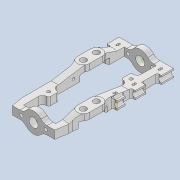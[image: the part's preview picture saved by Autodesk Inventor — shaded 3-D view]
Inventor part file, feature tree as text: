
AUTODESK INVENTOR PART (.ipt)
format: ipt  version: 2020 (Build 240168000, 168)  size: 925,184 bytes
history: native  units: mm
features: projected_geometry x23, sketch x22, extrude x20, thicken_offset x10, fillet x10, chamfer x7, other x5, plane x3, reference x3, hole x2
ambient origin geometry x8: Origin, YZ Plane, XZ Plane, XY Plane, X Axis, Y Axis, Z Axis, Center Point
bodies: Solid1 (feature_tree)
feature tree (105):
  extrude  "Extrusion1"  Depth=4.0mm
  plane  "Work Plane1"
  extrude  "Extrusion2"  Depth=2.0mm TaperAngle=0.0deg
  extrude  "Extrusion3"  Depth=4.0mm
  extrude  "Extrusion4"  Depth=2.0mm TaperAngle=0.0deg
  hole  "Hole1"  [1 undecoded]
  thicken_offset  "Thicken1"
  thicken_offset  "Thicken2"
  thicken_offset  "Thicken3"
  thicken_offset  "Thicken4"
  extrude  "Extrusion5"  Depth=3.0mm
  extrude  "Extrusion6"  Depth=2.0mm
  extrude  "Extrusion8"  Depth=6.0mm
  extrude  "Extrusion9"  Depth=3.5mm
  extrude  "Extrusion11"  Depth=3.5mm
  hole  "Hole2"  [1 undecoded]
  extrude  "Extrusion15"  Depth=3.5mm
  extrude  "Extrusion16"  Depth=3.5mm
  chamfer  "Chamfer1"  Distance=6.0mm
  chamfer  "Chamfer2"  Distance=2.0mm
  chamfer  "Chamfer3"  Distance=7.5mm
  chamfer  "Chamfer4"  Distance=9.0mm
  fillet  "Fillet4"  Radius=2.0mm
  fillet  "Fillet5"  Radius=3.25mm
  chamfer  "Chamfer5"  Distance=6.5mm
  fillet  "Fillet6"  Radius=6.0mm
  extrude  "Extrusion17"  Depth=2.0mm TaperAngle=0.0deg
  plane  "Work Plane3"
  extrude  "Extrusion18"  Depth=1.0mm
  plane  "Work Plane4"
  extrude  "Extrusion19"  Depth=3.0mm TaperAngle=0.0deg
  extrude  "Extrusion20"  Depth=3.0mm
  fillet  "Fillet8"  Radius=3.0mm
  fillet  "Fillet9"  Radius=3.0mm
  fillet  "Fillet10"  Radius=6.5mm
  extrude  "Extrusion21"  Depth=1.0mm
  extrude  "Extrusion22"  Depth=3.0mm TaperAngle=0.0deg
  thicken_offset  "Thicken9"
  thicken_offset  "Thicken10"
  thicken_offset  "Thicken11"
  thicken_offset  "Thicken12"
  extrude  "Extrusion23"  Depth=6.0mm
  fillet  "Fillet11"  Radius=2.0mm
  extrude  "Extrusion24"  Depth=6.0mm
  thicken_offset  "Thicken13"
  thicken_offset  "Thicken14"
  chamfer  "Chamfer7"  Distance=2.0mm
  chamfer  "Chamfer8"  Distance=2.0mm Angle=30.0deg
  fillet  "Fillet12"  Radius=5.0mm
  fillet  "Fillet13"  Radius=2.0mm
  fillet  "Fillet14"  Radius=5.0mm
  extrude  "Extrusion25"  Depth=1.0mm
  sketch  "Sketch1"  dims[d0=10.0mm d1=4.0mm]
  sketch  "Sketch2"  dims[d2=30.0mm d3=2.0mm d4=0.0mm]
  sketch  "Sketch3"  dims[d5=10.0mm d6=4.0mm]
  projected_geometry  "Projected Loop1"
  projected_geometry  "Projected Loop2"
  projected_geometry  "Projected Loop3"
  projected_geometry  "Projected Loop4"
  sketch  "Sketch4"  dims[d7=30.0mm d8=2.0mm d9=0.0mm]
  sketch  "Sketch5"  dims[d10=3.0mm d11=54.0mm]
  sketch  "Sketch6"  dims[d12=3.0mm d13=54.0mm]
  projected_geometry  "Projected Loop5"
  reference  "Reference1"
  reference  "Reference2"
  sketch  "Sketch7"  dims[d14=2.0mm d15=0.0mm d16=4.5mm]
  projected_geometry  "Projected Loop6"
  reference  "Reference3"
  sketch  "Sketch9"  dims[d17=2.0mm d18=0.0mm d19=6.0mm]
  projected_geometry  "Projected Loop9"
  sketch  "Sketch10"  dims[d20=6.0mm]
  projected_geometry  "Projected Loop10"
  sketch  "Sketch12"  dims[d21=1.6mm d22=6.0mm d23=4.0mm d24=2.0mm d25=90.0deg d26=100.0mm d27=0.0mm d28=3.5mm]
  projected_geometry  "Projected Loop13"
  sketch  "Sketch13"  dims[d29=3.5mm d30=3.5mm]
  projected_geometry  "Projected Loop14"
  sketch  "Sketch18"  dims[d31=3.5mm d32=3.5mm]
  projected_geometry  "Projected Loop20"
  sketch  "Sketch19"  dims[d33=3.5mm d34=3.5mm]
  projected_geometry  "Projected Loop21"
  sketch  "Sketch20"  dims[d35=3.5mm d36=7.5mm]
  projected_geometry  "Projected Loop22"
  sketch  "Sketch21"  dims[d37=9.0mm]
  projected_geometry  "Projected Loop23"
  sketch  "Sketch22"  dims[d38=3.0mm]
  projected_geometry  "Projected Loop24"
  sketch  "Sketch23"  dims[d39=3.25mm]
  projected_geometry  "Projected Loop25"
  sketch  "Sketch24"  dims[d40=3.25mm]
  projected_geometry  "Projected Loop26"
  sketch  "Sketch25"  dims[d41=6.0mm]
  projected_geometry  "Projected Loop27"
  sketch  "Sketch26"  dims[d42=6.0mm]
  projected_geometry  "Projected Loop28"
  projected_geometry  "Projected Loop29"
  sketch  "Sketch27"  dims[d43=2.0mm]
  projected_geometry  "Projected Loop30"
  projected_geometry  "Projected Loop31"
  sketch  "Sketch28"  dims[d44=6.5mm d45=6.0mm d46=2.0mm d47=0.0mm d48=7.5mm d49=9.0mm d50=2.0mm d51=3.25mm d52=6.5mm d53=6.0mm d54=2.0mm d55=0.0mm d60=7.0mm d61=3.0mm d62=0.0mm d66=3.0mm d67=3.0mm d68=3.0mm d69=0.0mm d76=6.5mm d77=7.0mm d78=3.0mm d79=0.0mm d80=3.0mm d81=6.0mm d82=4.0mm d83=2.0mm d84=90.0deg d85=100.0mm d86=0.0mm d107=6.0mm d108=2.0mm d109=0.0mm d110=6.0mm d111=2.0mm d112=0.0mm d113=12.0mm d114=2.0mm d115=30.0deg d116=5.0mm d117=2.0mm d118=30.0deg d119=12.0mm d120=2.0mm d121=30.0deg d122=5.0mm d123=2.0mm d124=30.0deg d125=1.0mm d126=8.0mm d127=1.0mm d128=2.0mm d129=30.0deg d130=0.5mm d135=2.5mm d136=2.0mm d137=4.0mm d138=5.0mm d139=0.0mm d140=8.0mm d141=5.0mm d142=0.0mm d143=9.0mm d144=4.0mm d145=0.0mm d146=2.5mm d147=2.0mm d148=4.0mm d149=5.0mm d150=0.0mm d151=1.0mm d152=1.0mm d153=1.0mm d154=3.0mm d155=2.0mm d156=3.0mm d157=2.0mm d158=3.0mm d159=2.0mm d160=0.5mm d161=1.0mm d162=0.5mm d163=1.0mm d164=0.5mm d165=1.0mm d166=8.0mm d167=0.0mm d168=3.0mm d169=0.5mm d170=1.0mm d171=8.0mm d172=0.0mm d173=0.5mm d174=0.5mm d175=0.5mm d176=0.5mm d177=0.5mm d178=0.5mm d179=0.5mm d180=0.5mm d181=12.0mm d182=1.5mm d183=3.0mm d184=5.0mm d185=12.0mm d186=1.5mm d187=3.0mm d188=5.0mm d189=8.0mm d190=0.0mm d191=2.0mm d192=2.5mm d193=1.6mm d194=2.5mm d195=1.6mm d196=8.0mm d197=0.0mm d198=1.0mm d199=1.0mm d200=1.0mm d201=1.0mm d202=1.0mm d203=6.0mm d204=30.0deg d205=1.0mm d206=6.0mm d207=30.0deg d208=4.0mm d209=4.0mm d210=1.0mm d211=1.0mm d212=1.4mm d213=8.0mm d214=0.0mm]
  projected_geometry  "Projected Loop32"
  parser-record x1  (decoder bookkeeping rows leaked as tree rows — omitted from the tree; the rows remain in map.json)
  other  "tip2_ass_t1.iam"
  other  "cab_coil_1:1"
  other  "cab_coil_1:2"
  other  "bearing_3_6_2:1"
note: 2 required parameter values undecoded (feature->parameter linkage not recoverable at this tier; creation-order binding heuristic only, values carry confidence <= 0.55)
note: 1 file-system path scrubbed to <path> (originals preserved in map.json)
